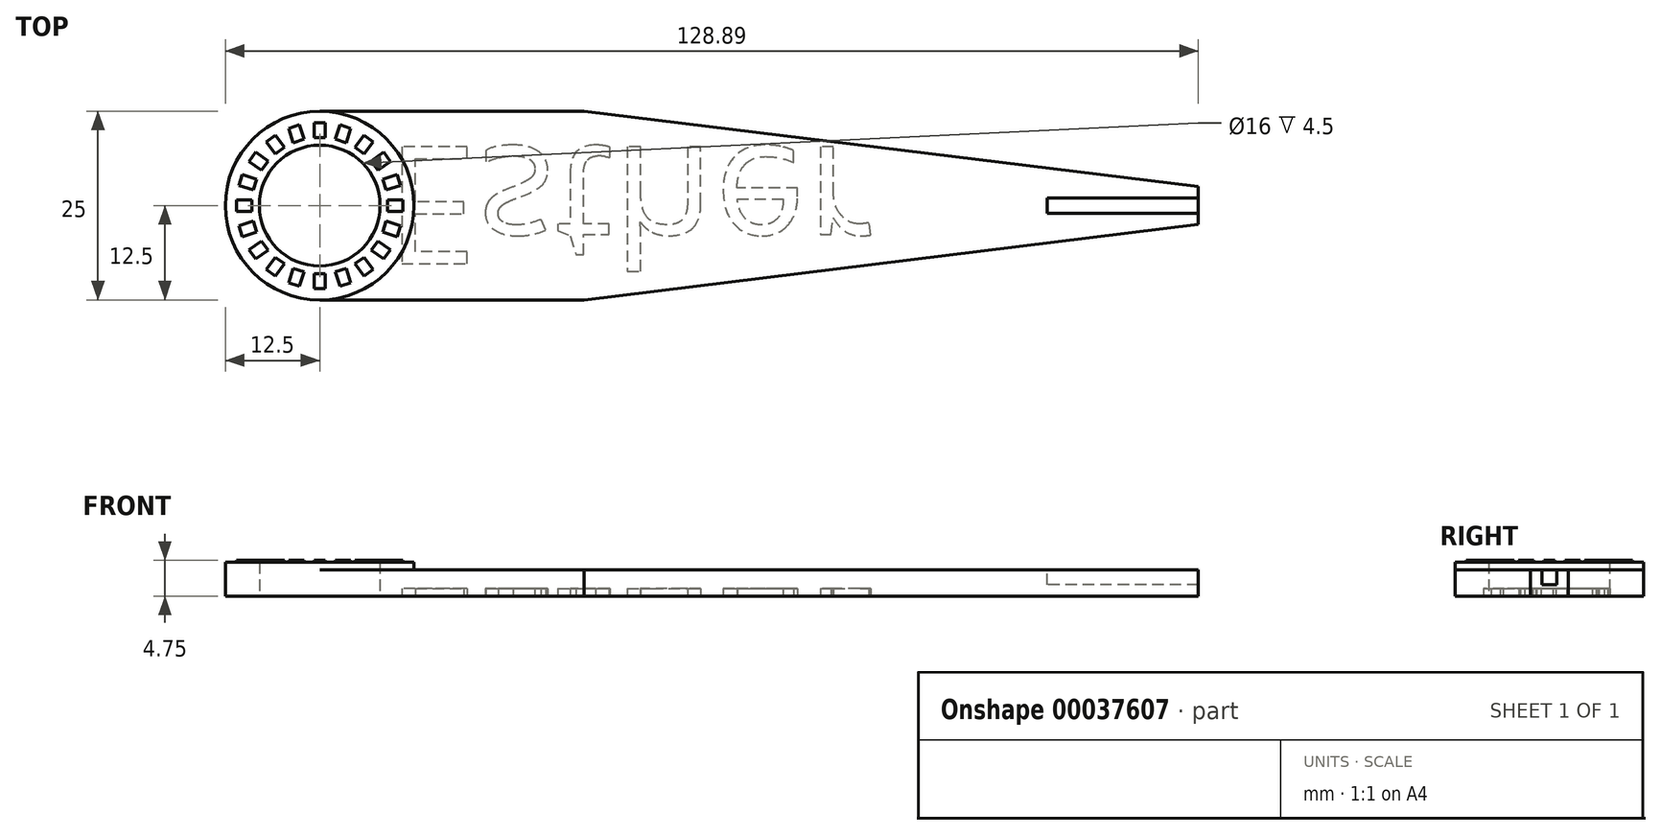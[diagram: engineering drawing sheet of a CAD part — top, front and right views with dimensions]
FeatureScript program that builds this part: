
annotation { "Feature Type Name" : "Feature", "Feature Type Description" : "" }
export const myFeature = defineFeature(function(context is Context, id is Id, definition is map)
    precondition{}
    {
        {
            var Q0;
            Q0=qCreatedBy(makeId("Top.planeOp"),FACE);
            var sketch = newSketch(context, id + "F0", { "sketchPlane" : qUnion([Q0])});
            skCircle(sketch, "E0", {"center": v(0, 0) * mm, "radius": 8 * mm});
            skCircle(sketch, "E1", {"center": v(0, 0) * mm, "radius": 12.5 * mm});
            skLineSegment(sketch, "E2", {"start": v(0, 12.5) * mm, "end": v(35, 12.5) * mm});
            skPoint(sketch, "E3", {"position": v(0, 12.5) * mm});
            skLineSegment(sketch, "E4", {"start": v(0, 0) * mm, "end": v(47.77, 0) * mm, "construction": true});
            skLineSegment(sketch, "E5.MirrorCS", {"start": v(0, -12.5) * mm, "end": v(35, -12.5) * mm});
            skLineSegment(sketch, "E6", {"start": v(35, 12.5) * mm, "end": v(79.85, 12.5) * mm, "construction": true});
            skLineSegment(sketch, "E7", {"start": v(35, 12.5) * mm, "end": v(116.39, 2.5) * mm});
            skLineSegment(sketch, "E8.MirrorCS", {"start": v(35, -12.5) * mm, "end": v(116.39, -2.5) * mm});
            skLineSegment(sketch, "E9", {"start": v(116.39, 2.5) * mm, "end": v(116.39, -2.5) * mm});
            skSolve(sketch);
        }
        {
            var Q0;
            Q0 = qSketchRegion(id + "F0", true);
            extrude(context, id + "F1", {"entities" : qUnion([Q0]), "depth" : 3.5 * mm});
        }
        {
            var Q0;
            Q0=makeQuery(id+"F1.opExtrude","CAP_FACE",FACE,{"disambiguationData":[OSD([sQuery(id+"F0.wireOp",EDGE,"E0"),sQuery(id+"F0.wireOp",EDGE,"E1"),sQuery(id+"F0.wireOp",EDGE,"E2"),sQuery(id+"F0.wireOp",EDGE,"E5.MirrorCS"),sQuery(id+"F0.wireOp",EDGE,"E7"),sQuery(id+"F0.wireOp",EDGE,"E8.MirrorCS"),sQuery(id+"F0.wireOp",EDGE,"E9")])],"isStart":false});
            var sketch = newSketch(context, id + "F2", { "sketchPlane" : qUnion([Q0])});
            skCircle(sketch, "E10", {"center": v(0, 0) * mm, "radius": 12.5 * mm});
            skCircle(sketch, "E11", {"center": v(0, 0) * mm, "radius": 8 * mm});
            skSolve(sketch);
        }
        {
            var Q0;
            Q0=makeQuery(id+"F2.imprint","IMPRINT",FACE,{"disambiguationData":[TD([[makeQuery(id+"F2.imprint","IMPRINT",EDGE,{"derivedFrom":sQuery(id+"F2.wireOp",EDGE,"E11")}),-1.0]])]});
            extrude(context, id + "F3", {"entities" : qUnion([Q0]), "operationType" : NewBodyOperationType.ADD, "depth" : 1 * mm});
        }
        {
            var Q0;
            Q0=makeQuery(id+"F3.opExtrude","CAP_FACE",FACE,{"disambiguationData":[OSD([sQuery(id+"F2.wireOp",EDGE,"E10"),sQuery(id+"F2.wireOp",EDGE,"E11")])],"isStart":false});
            var sketch = newSketch(context, id + "F4", { "sketchPlane" : qUnion([Q0])});
            skLineSegment(sketch, "E12.bottom", {"start": v(-0.75, 11) * mm, "end": v(0.75, 11) * mm});
            skLineSegment(sketch, "E12.top", {"start": v(-0.75, 9) * mm, "end": v(0.75, 9) * mm});
            skLineSegment(sketch, "E12.left", {"start": v(-0.75, 11) * mm, "end": v(-0.75, 9) * mm});
            skLineSegment(sketch, "E12.right", {"start": v(0.75, 11) * mm, "end": v(0.75, 9) * mm});
            skPoint(sketch, "E13", {"position": v(0, 8) * mm});
            skLineSegment(sketch, "E14.1.0", {"start": v(-4.11, 10.23) * mm, "end": v(-2.69, 10.7) * mm});
            skLineSegment(sketch, "E14.1.1", {"start": v(-4.11, 10.23) * mm, "end": v(-3.5, 8.33) * mm});
            skLineSegment(sketch, "E14.1.2", {"start": v(-3.5, 8.33) * mm, "end": v(-2.07, 8.8) * mm});
            skLineSegment(sketch, "E14.1.3", {"start": v(-2.69, 10.7) * mm, "end": v(-2.07, 8.8) * mm});
            skLineSegment(sketch, "E14.2.0", {"start": v(-7.07, 8.46) * mm, "end": v(-5.86, 9.34) * mm});
            skLineSegment(sketch, "E14.2.1", {"start": v(-7.07, 8.46) * mm, "end": v(-5.9, 6.84) * mm});
            skLineSegment(sketch, "E14.2.2", {"start": v(-5.9, 6.84) * mm, "end": v(-4.68, 7.72) * mm});
            skLineSegment(sketch, "E14.2.3", {"start": v(-5.86, 9.34) * mm, "end": v(-4.68, 7.72) * mm});
            skLineSegment(sketch, "E14.3.0", {"start": v(-9.34, 5.86) * mm, "end": v(-8.46, 7.07) * mm});
            skLineSegment(sketch, "E14.3.1", {"start": v(-9.34, 5.86) * mm, "end": v(-7.72, 4.68) * mm});
            skLineSegment(sketch, "E14.3.2", {"start": v(-7.72, 4.68) * mm, "end": v(-6.84, 5.9) * mm});
            skLineSegment(sketch, "E14.3.3", {"start": v(-8.46, 7.07) * mm, "end": v(-6.84, 5.9) * mm});
            skLineSegment(sketch, "E14.4.0", {"start": v(-10.7, 2.69) * mm, "end": v(-10.23, 4.11) * mm});
            skLineSegment(sketch, "E14.4.1", {"start": v(-10.7, 2.69) * mm, "end": v(-8.8, 2.07) * mm});
            skLineSegment(sketch, "E14.4.2", {"start": v(-8.8, 2.07) * mm, "end": v(-8.33, 3.5) * mm});
            skLineSegment(sketch, "E14.4.3", {"start": v(-10.23, 4.11) * mm, "end": v(-8.33, 3.5) * mm});
            skLineSegment(sketch, "E14.5.0", {"start": v(-11, -0.75) * mm, "end": v(-11, 0.75) * mm});
            skLineSegment(sketch, "E14.5.1", {"start": v(-11, -0.75) * mm, "end": v(-9, -0.75) * mm});
            skLineSegment(sketch, "E14.5.2", {"start": v(-9, -0.75) * mm, "end": v(-9, 0.75) * mm});
            skLineSegment(sketch, "E14.5.3", {"start": v(-11, 0.75) * mm, "end": v(-9, 0.75) * mm});
            skLineSegment(sketch, "E14.6.0", {"start": v(-10.23, -4.11) * mm, "end": v(-10.7, -2.69) * mm});
            skLineSegment(sketch, "E14.6.1", {"start": v(-10.23, -4.11) * mm, "end": v(-8.33, -3.5) * mm});
            skLineSegment(sketch, "E14.6.2", {"start": v(-8.33, -3.5) * mm, "end": v(-8.8, -2.07) * mm});
            skLineSegment(sketch, "E14.6.3", {"start": v(-10.7, -2.69) * mm, "end": v(-8.8, -2.07) * mm});
            skLineSegment(sketch, "E14.7.0", {"start": v(-8.46, -7.07) * mm, "end": v(-9.34, -5.86) * mm});
            skLineSegment(sketch, "E14.7.1", {"start": v(-8.46, -7.07) * mm, "end": v(-6.84, -5.9) * mm});
            skLineSegment(sketch, "E14.7.2", {"start": v(-6.84, -5.9) * mm, "end": v(-7.72, -4.68) * mm});
            skLineSegment(sketch, "E14.7.3", {"start": v(-9.34, -5.86) * mm, "end": v(-7.72, -4.68) * mm});
            skLineSegment(sketch, "E14.8.0", {"start": v(-5.86, -9.34) * mm, "end": v(-7.07, -8.46) * mm});
            skLineSegment(sketch, "E14.8.1", {"start": v(-5.86, -9.34) * mm, "end": v(-4.68, -7.72) * mm});
            skLineSegment(sketch, "E14.8.2", {"start": v(-4.68, -7.72) * mm, "end": v(-5.9, -6.84) * mm});
            skLineSegment(sketch, "E14.8.3", {"start": v(-7.07, -8.46) * mm, "end": v(-5.9, -6.84) * mm});
            skLineSegment(sketch, "E14.9.0", {"start": v(-2.69, -10.7) * mm, "end": v(-4.11, -10.23) * mm});
            skLineSegment(sketch, "E14.9.1", {"start": v(-2.69, -10.7) * mm, "end": v(-2.07, -8.8) * mm});
            skLineSegment(sketch, "E14.9.2", {"start": v(-2.07, -8.8) * mm, "end": v(-3.5, -8.33) * mm});
            skLineSegment(sketch, "E14.9.3", {"start": v(-4.11, -10.23) * mm, "end": v(-3.5, -8.33) * mm});
            skLineSegment(sketch, "E14.10.0", {"start": v(0.75, -11) * mm, "end": v(-0.75, -11) * mm});
            skLineSegment(sketch, "E14.10.1", {"start": v(0.75, -11) * mm, "end": v(0.75, -9) * mm});
            skLineSegment(sketch, "E14.10.2", {"start": v(0.75, -9) * mm, "end": v(-0.75, -9) * mm});
            skLineSegment(sketch, "E14.10.3", {"start": v(-0.75, -11) * mm, "end": v(-0.75, -9) * mm});
            skLineSegment(sketch, "E14.11.0", {"start": v(4.11, -10.23) * mm, "end": v(2.69, -10.7) * mm});
            skLineSegment(sketch, "E14.11.1", {"start": v(4.11, -10.23) * mm, "end": v(3.5, -8.33) * mm});
            skLineSegment(sketch, "E14.11.2", {"start": v(3.5, -8.33) * mm, "end": v(2.07, -8.8) * mm});
            skLineSegment(sketch, "E14.11.3", {"start": v(2.69, -10.7) * mm, "end": v(2.07, -8.8) * mm});
            skLineSegment(sketch, "E14.12.0", {"start": v(7.07, -8.46) * mm, "end": v(5.86, -9.34) * mm});
            skLineSegment(sketch, "E14.12.1", {"start": v(7.07, -8.46) * mm, "end": v(5.9, -6.84) * mm});
            skLineSegment(sketch, "E14.12.2", {"start": v(5.9, -6.84) * mm, "end": v(4.68, -7.72) * mm});
            skLineSegment(sketch, "E14.12.3", {"start": v(5.86, -9.34) * mm, "end": v(4.68, -7.72) * mm});
            skLineSegment(sketch, "E14.13.0", {"start": v(9.34, -5.86) * mm, "end": v(8.46, -7.07) * mm});
            skLineSegment(sketch, "E14.13.1", {"start": v(9.34, -5.86) * mm, "end": v(7.72, -4.68) * mm});
            skLineSegment(sketch, "E14.13.2", {"start": v(7.72, -4.68) * mm, "end": v(6.84, -5.9) * mm});
            skLineSegment(sketch, "E14.13.3", {"start": v(8.46, -7.07) * mm, "end": v(6.84, -5.9) * mm});
            skLineSegment(sketch, "E14.14.0", {"start": v(10.7, -2.69) * mm, "end": v(10.23, -4.11) * mm});
            skLineSegment(sketch, "E14.14.1", {"start": v(10.7, -2.69) * mm, "end": v(8.8, -2.07) * mm});
            skLineSegment(sketch, "E14.14.2", {"start": v(8.8, -2.07) * mm, "end": v(8.33, -3.5) * mm});
            skLineSegment(sketch, "E14.14.3", {"start": v(10.23, -4.11) * mm, "end": v(8.33, -3.5) * mm});
            skLineSegment(sketch, "E14.15.0", {"start": v(11, 0.75) * mm, "end": v(11, -0.75) * mm});
            skLineSegment(sketch, "E14.15.1", {"start": v(11, 0.75) * mm, "end": v(9, 0.75) * mm});
            skLineSegment(sketch, "E14.15.2", {"start": v(9, 0.75) * mm, "end": v(9, -0.75) * mm});
            skLineSegment(sketch, "E14.15.3", {"start": v(11, -0.75) * mm, "end": v(9, -0.75) * mm});
            skLineSegment(sketch, "E14.16.0", {"start": v(10.23, 4.11) * mm, "end": v(10.7, 2.69) * mm});
            skLineSegment(sketch, "E14.16.1", {"start": v(10.23, 4.11) * mm, "end": v(8.33, 3.5) * mm});
            skLineSegment(sketch, "E14.16.2", {"start": v(8.33, 3.5) * mm, "end": v(8.8, 2.07) * mm});
            skLineSegment(sketch, "E14.16.3", {"start": v(10.7, 2.69) * mm, "end": v(8.8, 2.07) * mm});
            skLineSegment(sketch, "E14.17.0", {"start": v(8.46, 7.07) * mm, "end": v(9.34, 5.86) * mm});
            skLineSegment(sketch, "E14.17.1", {"start": v(8.46, 7.07) * mm, "end": v(6.84, 5.9) * mm});
            skLineSegment(sketch, "E14.17.2", {"start": v(6.84, 5.9) * mm, "end": v(7.72, 4.68) * mm});
            skLineSegment(sketch, "E14.17.3", {"start": v(9.34, 5.86) * mm, "end": v(7.72, 4.68) * mm});
            skLineSegment(sketch, "E14.18.0", {"start": v(5.86, 9.34) * mm, "end": v(7.07, 8.46) * mm});
            skLineSegment(sketch, "E14.18.1", {"start": v(5.86, 9.34) * mm, "end": v(4.68, 7.72) * mm});
            skLineSegment(sketch, "E14.18.2", {"start": v(4.68, 7.72) * mm, "end": v(5.9, 6.84) * mm});
            skLineSegment(sketch, "E14.18.3", {"start": v(7.07, 8.46) * mm, "end": v(5.9, 6.84) * mm});
            skLineSegment(sketch, "E14.19.0", {"start": v(2.69, 10.7) * mm, "end": v(4.11, 10.23) * mm});
            skLineSegment(sketch, "E14.19.1", {"start": v(2.69, 10.7) * mm, "end": v(2.07, 8.8) * mm});
            skLineSegment(sketch, "E14.19.2", {"start": v(2.07, 8.8) * mm, "end": v(3.5, 8.33) * mm});
            skLineSegment(sketch, "E14.19.3", {"start": v(4.11, 10.23) * mm, "end": v(3.5, 8.33) * mm});
            skPoint(sketch, "E14.center", {"position": v(0, 0) * mm});
            skSolve(sketch);
        }
        {
            var Q0;
            Q0=makeQuery(id+"F4.imprint","IMPRINT",FACE,{"disambiguationData":[TD([[makeQuery(id+"F4.imprint","IMPRINT",EDGE,{"derivedFrom":sQuery(id+"F4.wireOp",EDGE,"E12.bottom")}),-1.0]])]});
            var Q1;
            Q1=makeQuery(id+"F4.imprint","IMPRINT",FACE,{"disambiguationData":[TD([[makeQuery(id+"F4.imprint","IMPRINT",EDGE,{"derivedFrom":sQuery(id+"F4.wireOp",EDGE,"E14.1.0")}),-1.0]])]});
            var Q2;
            Q2=makeQuery(id+"F4.imprint","IMPRINT",FACE,{"disambiguationData":[TD([[makeQuery(id+"F4.imprint","IMPRINT",EDGE,{"derivedFrom":sQuery(id+"F4.wireOp",EDGE,"E14.2.0")}),-1.0]])]});
            var Q3;
            Q3=makeQuery(id+"F4.imprint","IMPRINT",FACE,{"disambiguationData":[TD([[makeQuery(id+"F4.imprint","IMPRINT",EDGE,{"derivedFrom":sQuery(id+"F4.wireOp",EDGE,"E14.3.0")}),-1.0]])]});
            var Q4;
            Q4=makeQuery(id+"F4.imprint","IMPRINT",FACE,{"disambiguationData":[TD([[makeQuery(id+"F4.imprint","IMPRINT",EDGE,{"derivedFrom":sQuery(id+"F4.wireOp",EDGE,"E14.5.0")}),-1.0]])]});
            var Q5;
            Q5=makeQuery(id+"F4.imprint","IMPRINT",FACE,{"disambiguationData":[TD([[makeQuery(id+"F4.imprint","IMPRINT",EDGE,{"derivedFrom":sQuery(id+"F4.wireOp",EDGE,"E14.6.0")}),-1.0]])]});
            var Q6;
            Q6=makeQuery(id+"F4.imprint","IMPRINT",FACE,{"disambiguationData":[TD([[makeQuery(id+"F4.imprint","IMPRINT",EDGE,{"derivedFrom":sQuery(id+"F4.wireOp",EDGE,"E14.7.0")}),-1.0]])]});
            var Q7;
            Q7=makeQuery(id+"F4.imprint","IMPRINT",FACE,{"disambiguationData":[TD([[makeQuery(id+"F4.imprint","IMPRINT",EDGE,{"derivedFrom":sQuery(id+"F4.wireOp",EDGE,"E14.8.0")}),-1.0]])]});
            var Q8;
            Q8=makeQuery(id+"F4.imprint","IMPRINT",FACE,{"disambiguationData":[TD([[makeQuery(id+"F4.imprint","IMPRINT",EDGE,{"derivedFrom":sQuery(id+"F4.wireOp",EDGE,"E14.9.0")}),-1.0]])]});
            var Q9;
            Q9=makeQuery(id+"F4.imprint","IMPRINT",FACE,{"disambiguationData":[TD([[makeQuery(id+"F4.imprint","IMPRINT",EDGE,{"derivedFrom":sQuery(id+"F4.wireOp",EDGE,"E14.10.0")}),-1.0]])]});
            var Q10;
            Q10=makeQuery(id+"F4.imprint","IMPRINT",FACE,{"disambiguationData":[TD([[makeQuery(id+"F4.imprint","IMPRINT",EDGE,{"derivedFrom":sQuery(id+"F4.wireOp",EDGE,"E14.11.0")}),-1.0]])]});
            var Q11;
            Q11=makeQuery(id+"F4.imprint","IMPRINT",FACE,{"disambiguationData":[TD([[makeQuery(id+"F4.imprint","IMPRINT",EDGE,{"derivedFrom":sQuery(id+"F4.wireOp",EDGE,"E14.12.0")}),-1.0]])]});
            var Q12;
            Q12=makeQuery(id+"F4.imprint","IMPRINT",FACE,{"disambiguationData":[TD([[makeQuery(id+"F4.imprint","IMPRINT",EDGE,{"derivedFrom":sQuery(id+"F4.wireOp",EDGE,"E14.13.0")}),-1.0]])]});
            var Q13;
            Q13=makeQuery(id+"F4.imprint","IMPRINT",FACE,{"disambiguationData":[TD([[makeQuery(id+"F4.imprint","IMPRINT",EDGE,{"derivedFrom":sQuery(id+"F4.wireOp",EDGE,"E14.14.0")}),-1.0]])]});
            var Q14;
            Q14=makeQuery(id+"F4.imprint","IMPRINT",FACE,{"disambiguationData":[TD([[makeQuery(id+"F4.imprint","IMPRINT",EDGE,{"derivedFrom":sQuery(id+"F4.wireOp",EDGE,"E14.15.0")}),-1.0]])]});
            var Q15;
            Q15=makeQuery(id+"F4.imprint","IMPRINT",FACE,{"disambiguationData":[TD([[makeQuery(id+"F4.imprint","IMPRINT",EDGE,{"derivedFrom":sQuery(id+"F4.wireOp",EDGE,"E14.16.0")}),-1.0]])]});
            var Q16;
            Q16=makeQuery(id+"F4.imprint","IMPRINT",FACE,{"disambiguationData":[TD([[makeQuery(id+"F4.imprint","IMPRINT",EDGE,{"derivedFrom":sQuery(id+"F4.wireOp",EDGE,"E14.17.0")}),-1.0]])]});
            var Q17;
            Q17=makeQuery(id+"F4.imprint","IMPRINT",FACE,{"disambiguationData":[TD([[makeQuery(id+"F4.imprint","IMPRINT",EDGE,{"derivedFrom":sQuery(id+"F4.wireOp",EDGE,"E14.18.0")}),-1.0]])]});
            var Q18;
            Q18=makeQuery(id+"F4.imprint","IMPRINT",FACE,{"disambiguationData":[TD([[makeQuery(id+"F4.imprint","IMPRINT",EDGE,{"derivedFrom":sQuery(id+"F4.wireOp",EDGE,"E14.19.0")}),-1.0]])]});
            var Q19;
            Q19=makeQuery(id+"F4.imprint","IMPRINT",FACE,{"disambiguationData":[TD([[makeQuery(id+"F4.imprint","IMPRINT",EDGE,{"derivedFrom":sQuery(id+"F4.wireOp",EDGE,"E14.4.0")}),-1.0]])]});
            extrude(context, id + "F5", {"entities" : qUnion([Q0, Q1, Q2, Q3, Q4, Q5, Q6, Q7, Q8, Q9, Q10, Q11, Q12, Q13, Q14, Q15, Q16, Q17, Q18, Q19]), "operationType" : NewBodyOperationType.ADD, "depth" : .25 * mm});
        }
        {
            var Q0;
            Q0=makeQuery(id+"F1.opExtrude","CAP_FACE",FACE,{"disambiguationData":[OSD([sQuery(id+"F0.wireOp",EDGE,"E0"),sQuery(id+"F0.wireOp",EDGE,"E1"),sQuery(id+"F0.wireOp",EDGE,"E2"),sQuery(id+"F0.wireOp",EDGE,"E5.MirrorCS"),sQuery(id+"F0.wireOp",EDGE,"E7"),sQuery(id+"F0.wireOp",EDGE,"E8.MirrorCS"),sQuery(id+"F0.wireOp",EDGE,"E9")])],"isStart":false});
            var sketch = newSketch(context, id + "F6", { "sketchPlane" : qUnion([Q0])});
            skLineSegment(sketch, "E15.bottom", {"start": v(116.39, 1) * mm, "end": v(96.39, 1) * mm});
            skLineSegment(sketch, "E15.top", {"start": v(116.39, -1) * mm, "end": v(96.39, -1) * mm});
            skLineSegment(sketch, "E15.left", {"start": v(116.39, 1) * mm, "end": v(116.39, -1) * mm});
            skLineSegment(sketch, "E15.right", {"start": v(96.39, 1) * mm, "end": v(96.39, -1) * mm});
            skSolve(sketch);
        }
        {
            var Q0;
            Q0=makeQuery(id+"F6.imprint","IMPRINT",FACE,{"disambiguationData":[TD([[makeQuery(id+"F6.imprint","IMPRINT",EDGE,{"derivedFrom":sQuery(id+"F6.wireOp",EDGE,"E15.bottom")}),1.0]])]});
            extrude(context, id + "F7", {"entities" : qUnion([Q0]), "operationType" : NewBodyOperationType.REMOVE, "oppositeDirection" : true, "depth" : 2 * mm});
        }
        {
            var Q0;
            Q0=makeQuery(id+"F1.opExtrude","CAP_FACE",FACE,{"disambiguationData":[OSD([sQuery(id+"F0.wireOp",EDGE,"E0"),sQuery(id+"F0.wireOp",EDGE,"E1"),sQuery(id+"F0.wireOp",EDGE,"E2"),sQuery(id+"F0.wireOp",EDGE,"E5.MirrorCS"),sQuery(id+"F0.wireOp",EDGE,"E7"),sQuery(id+"F0.wireOp",EDGE,"E8.MirrorCS"),sQuery(id+"F0.wireOp",EDGE,"E9")])],"isStart":true});
            var sketch = newSketch(context, id + "F8", { "sketchPlane" : qUnion([Q0])});
            skText(sketch, "E16", { "text": "Esther", "fontName": "OpenSans-Regular.ttf"});
            skPoint(sketch, "E17", {"position": v(75.7, 7.5) * mm});
            const initialGuessF8  = {"E16": [0.00873, -0.00783, 1, 0, 0.01566]};
            skSetInitialGuess(sketch, initialGuessF8);
            skSolve(sketch);
        }
        {
            var Q0;
            Q0 = qSketchRegion(id + "F8", true);
            extrude(context, id + "F9", {"entities" : qUnion([Q0]), "operationType" : NewBodyOperationType.REMOVE, "oppositeDirection" : true, "depth" : 1 * mm});
        }
    });
